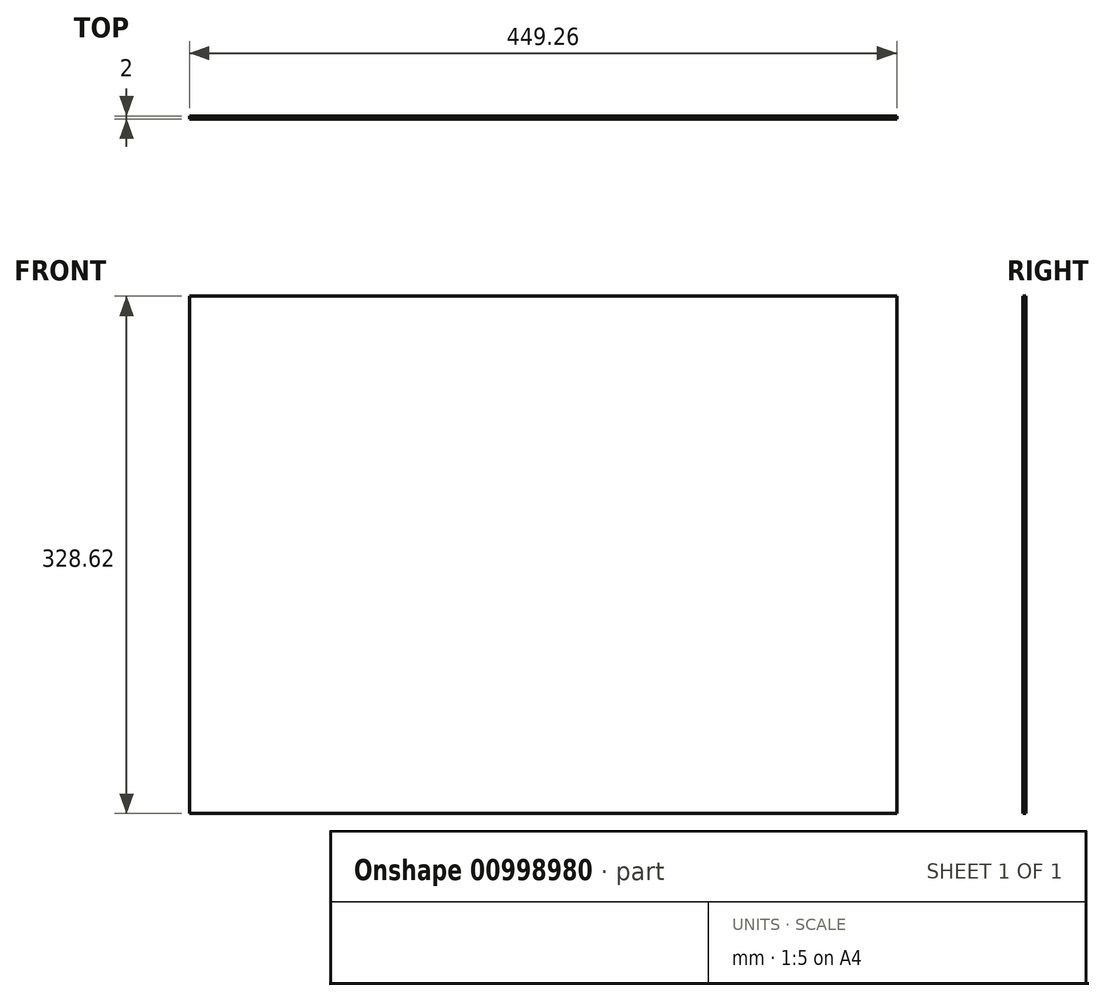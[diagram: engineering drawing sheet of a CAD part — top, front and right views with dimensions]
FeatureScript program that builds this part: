
annotation { "Feature Type Name" : "Feature", "Feature Type Description" : "" }
export const myFeature = defineFeature(function(context is Context, id is Id, definition is map)
    precondition{}
    {
        {
            var Q0;
            Q0=qCreatedBy(makeId("Front.planeOp"),FACE);
            var sketch = newSketch(context, id + "F0", { "sketchPlane" : qUnion([Q0])});
            skLineSegment(sketch, "E0.bottom", {"start": v(224.63, -164.3) * mm, "end": v(-224.63, -164.3) * mm});
            skLineSegment(sketch, "E0.top", {"start": v(224.63, 164.3) * mm, "end": v(-224.63, 164.3) * mm});
            skLineSegment(sketch, "E0.left", {"start": v(224.63, -164.3) * mm, "end": v(224.63, 164.3) * mm});
            skLineSegment(sketch, "E0.right", {"start": v(-224.63, -164.3) * mm, "end": v(-224.63, 164.3) * mm});
            skPoint(sketch, "E0.middle", {"position": v(0, 0) * mm});
            skSolve(sketch);
        }
        {
            var Q0;
            Q0=makeQuery(id+"F0.imprint","IMPRINT",FACE,{"disambiguationData":[TD([[makeQuery(id+"F0.imprint","IMPRINT",EDGE,{"derivedFrom":sQuery(id+"F0.wireOp",EDGE,"E0.bottom")}),-1.0]])]});
            extrude(context, id + "F1", {"entities" : qUnion([Q0]), "depth" : 2 * mm, "offsetDistance" : 25.4 * mm});
        }
    });
